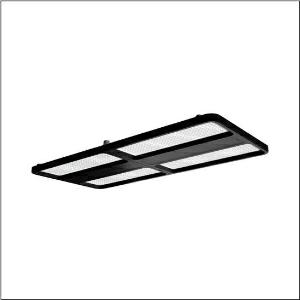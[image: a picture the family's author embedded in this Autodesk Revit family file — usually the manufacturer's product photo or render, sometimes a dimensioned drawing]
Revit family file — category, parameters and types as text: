
# Revit family: highbay_21_maxi_52hn32db4qda
name_source: partatom
category: Lighting Fixtures
units: mm (PartAtom-declared; Revit-internal decimal feet)

## family parameters
Cut with Voids When Loaded = No
Host = Face
Light Source = No
Part Type = Normal
Room Calculation Point = No
Round Connector Dimension = Use Diameter
Shared = No

## types (1)
- --- (1 x LED, 5840 lm, 31.4 W, 4000K)
    Apparent Load = 31 VA
    CIE Flux Codes = 90 98 100 100 100
    Color Rendering = 80
    Color Temperature = 4000K
    Default Elevation = 1800 mm
    Description = high bay luminaire Highbay 21 maxi; direct symmetric wide distribution, light control with lens of PMMA; UGR ≤ 22 (X = 4H | Y = 8H | S = 0.25H | reflection values 70/50/20); luminous flux: 38.000lm; light colour: 840, colour temperature: 4000K, MacAdam ≤ 3 SDCM (initial), colour rendering: CRI > 80; luminous efficacy: 192,2lm/W; rated service life: 75.000h (L80) at AT= ta max; control: DALI 2; luminaire connection: terminal, 5-pole, max. 2.5mm² (cable entry for one cable, Ø 8.5..16mm); mains connection: 230..240V, AC/DC 0/50..60Hz; connected load: 197,7W; protection rating (complete): IP66; insulation class (complete): insulation class I (protective earthing); protection symbol: D; impact resistance: IK08; certification: CE, ENEC, VDE, UKCA; luminaire for central battery installations according to EN 60598-2-22, internal wiring halogen-free; luminaire LABS conformity tested according to VDMA 24364:2018-05; Suitable for use in the food industry according to the specifications of IFS-Food, HACCP and/or BRC; housing frame of high-performance plastic PA6, matt jet black (RAL 9005); cover of PMMA; dimension (LxWxH): 946 x 442 x 72mm; permissible operating ambient temperature: -40..+60°C (reducing of maximum allowable ambient temperature of 5°C with ceiling mounting); packaging unit: 1 piece; (delivery without accessories; please order mounting accessories separately)
    Height = 72 mm  [stored 0.23622 ft]
    Lamp = 1 x LED
    Lamp Light Flux = 5840 lm
    Lamp Power = 31.4 W
    Lamp count = 1
    Length = 946 mm
    Luminous efficacy = 186 lm/W
    Manufacturer = Siteco
    ModVariant = No
    Model = 52HN32DB4QDA
    Mounting Place = Ceiling
    Mounting Type = Pendant
    Number of Poles = 1
    OnlyDefault = Yes
    Power Factor = 1
    Product Name = Highbay 21 maxi
    Product group = high bay luminaire
    ProductGroupID = 902
    Protection Class = Protection class I
    Protection Degree = IP 66
    RLX_Detail_Level = 1
    RLX_Emergency_Light_Flux = 0 lm
    RLX_Emergency_Type = 0
    RLX_Emergency_Type_DB = No
    RlxData = <blob elided: 133161 chars, md5=57687f6a>
    Socket = socket
    Standby Power = 0 W
    System Light Flux = 5840 lm
    System Power = 31 W
    Type Comments = : DC mode (central or group accumulator) initial emergency light level
    Type Image = l_1378821.jpg
    URL = http://relux.com
    VarID = @adj_019275
    Voltage = 0 V
    Weight = 0.00 kg
    Width = 442 mm

note: [stored X ft] marks values corroborated as IEEE doubles in the binary element streams (Revit-internal decimal feet)

## geometry (parser evidence)
native form markers: Blend x4, Sweep x10
no freeform markers — native parametric forms only
